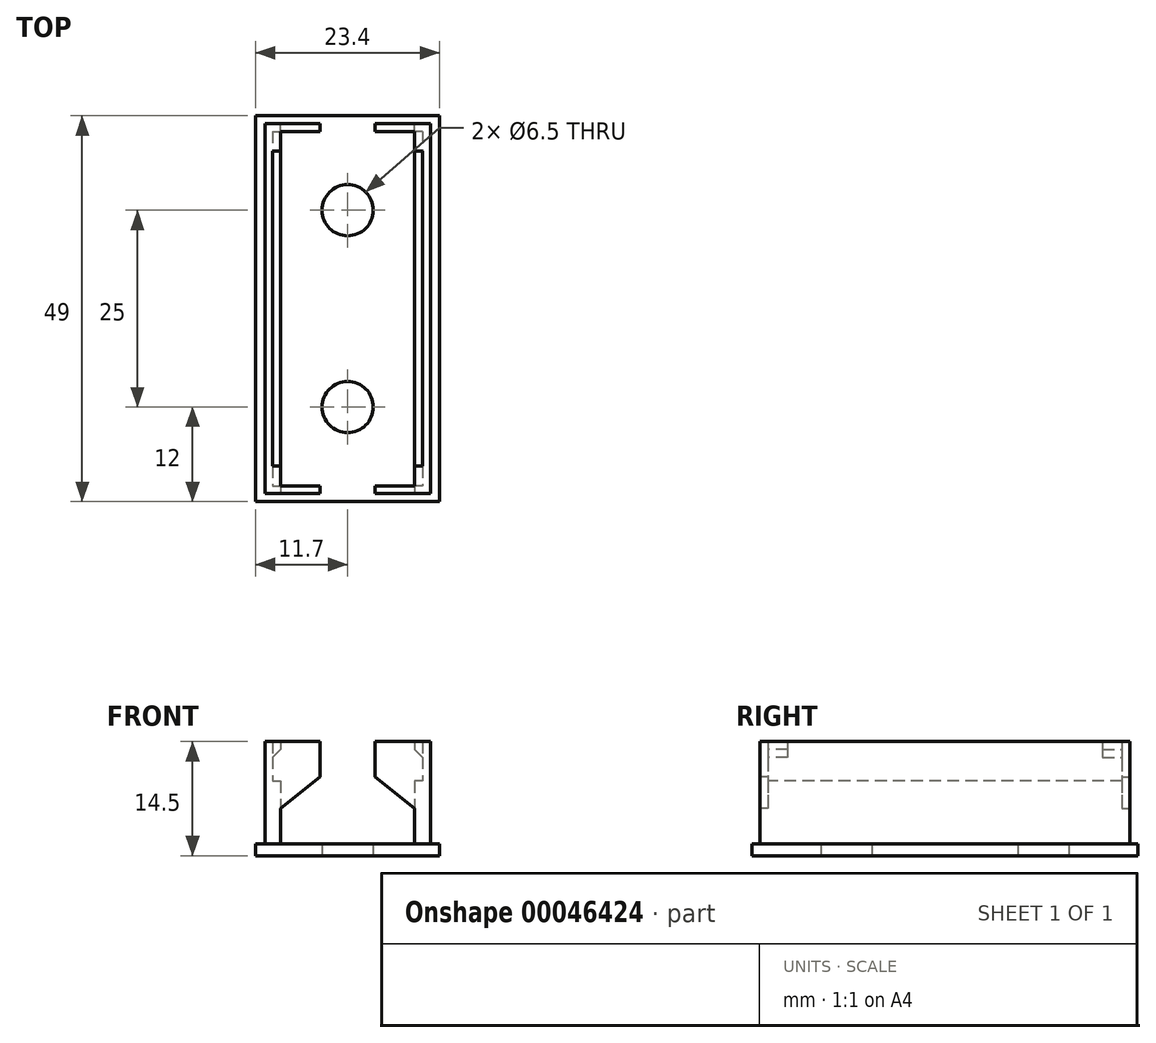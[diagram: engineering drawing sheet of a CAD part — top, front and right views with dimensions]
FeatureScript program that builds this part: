
annotation { "Feature Type Name" : "Feature", "Feature Type Description" : "" }
export const myFeature = defineFeature(function(context is Context, id is Id, definition is map)
    precondition{}
    {
        {
            var Q0;
            Q0=qCreatedBy(makeId("Top.planeOp"),FACE);
            var sketch = newSketch(context, id + "F0", { "sketchPlane" : qUnion([Q0])});
            skPoint(sketch, "E0.middle", {"position": v(0, 0) * mm});
            skCircle(sketch, "E1", {"center": v(0, 12.5) * mm, "radius": 3.25 * mm});
            skLineSegment(sketch, "E2", {"start": v(-11.7, 24.5) * mm, "end": v(-11.7, 0) * mm});
            skLineSegment(sketch, "E3", {"start": v(-11.7, 0) * mm, "end": v(0, 0) * mm});
            skLineSegment(sketch, "E4", {"start": v(-11.7, 24.5) * mm, "end": v(0, 24.5) * mm});
            skLineSegment(sketch, "E5", {"start": v(0, 24.5) * mm, "end": v(0, 0) * mm});
            skSolve(sketch);
        }
        {
            var Q0;
            Q0=makeQuery(id+"F0.imprint","IMPRINT",FACE,{"disambiguationData":[TD([[makeQuery(id+"F0.imprint","IMPRINT",EDGE,{"derivedFrom":sQuery(id+"F0.wireOp",EDGE,"E0.bottom")}),-1.0]])]});
            var Q1;
            Q1=makeQuery(id+"F0.imprint","IMPRINT",FACE,{"disambiguationData":[TD([[makeQuery(id+"F0.imprint","IMPRINT",EDGE,{"derivedFrom":sQuery(id+"F0.wireOp",EDGE,"E2")}),1.0]])]});
            extrude(context, id + "F1", {"entities" : qUnion([Q0, Q1]), "depth" : 1.5 * mm, "offsetDistance" : 25 * mm});
        }
        {
            var Q0;
            Q0=makeQuery(id+"F1.opExtrude","CAP_FACE",FACE,{"disambiguationData":[OSD([sQuery(id+"F0.wireOp",EDGE,"E0.bottom"),sQuery(id+"F0.wireOp",EDGE,"E0.top"),sQuery(id+"F0.wireOp",EDGE,"E0.left"),sQuery(id+"F0.wireOp",EDGE,"E0.right"),sQuery(id+"F0.wireOp",EDGE,"E1"),sQuery(id+"F0.wireOp",EDGE,"b4a6264c-28c6-449c-b6e5-1ad2d47b1fbf0.MirrorC")])],"isStart":false});
            var sketch = newSketch(context, id + "F2", { "sketchPlane" : qUnion([Q0])});
            skLineSegment(sketch, "E6.bottom", {"start": v(-10.5, 23.5) * mm, "end": v(-8.5, 23.5) * mm});
            skLineSegment(sketch, "E6.top", {"start": v(-10.5, 0) * mm, "end": v(-8.5, 0) * mm});
            skLineSegment(sketch, "E6.left", {"start": v(-10.5, 23.5) * mm, "end": v(-10.5, 0) * mm});
            skLineSegment(sketch, "E6.right", {"start": v(-8.5, 23.5) * mm, "end": v(-8.5, 0) * mm});
            skSolve(sketch);
        }
        {
            var Q0;
            Q0=makeQuery(id+"F2.imprint","IMPRINT",FACE,{"disambiguationData":[TD([[makeQuery(id+"F2.imprint","IMPRINT",EDGE,{"derivedFrom":sQuery(id+"F2.wireOp",EDGE,"4ac17364-d6f0-4829-a121-ceda3a2869c10.MirrorCS")}),1.0]])]});
            var Q1;
            Q1=makeQuery(id+"F2.imprint","IMPRINT",FACE,{"disambiguationData":[TD([[makeQuery(id+"F2.imprint","IMPRINT",EDGE,{"derivedFrom":sQuery(id+"F2.wireOp",EDGE,"E6.bottom")}),-1.0]])]});
            extrude(context, id + "F3", {"entities" : qUnion([Q0, Q1]), "operationType" : NewBodyOperationType.ADD, "depth" : 8 * mm, "offsetDistance" : 25 * mm});
        }
        {
            var Q0;
            Q0=makeQuery(id+"F3.opExtrude","CAP_FACE",FACE,{"disambiguationData":[OSD([sQuery(id+"F2.wireOp",EDGE,"E6.bottom"),sQuery(id+"F2.wireOp",EDGE,"E6.left"),sQuery(id+"F2.wireOp",EDGE,"E6.right"),sQuery(id+"F2.wireOp",EDGE,"4ac17364-d6f0-4829-a121-ceda3a2869c10.MirrorCS"),sQuery(id+"F2.wireOp",EDGE,"4ac17364-d6f0-4829-a121-ceda3a2869c12.MirrorCS"),sQuery(id+"F2.wireOp",EDGE,"4ac17364-d6f0-4829-a121-ceda3a2869c13.MirrorCS")])],"isStart":false});
            var sketch = newSketch(context, id + "F4", { "sketchPlane" : qUnion([Q0])});
            skLineSegment(sketch, "E7.bottom", {"start": v(-10.5, 23.5) * mm, "end": v(-9.5, 23.5) * mm});
            skLineSegment(sketch, "E7.top", {"start": v(-10.5, 0) * mm, "end": v(-9.5, 0) * mm});
            skLineSegment(sketch, "E7.left", {"start": v(-10.5, 23.5) * mm, "end": v(-10.5, 0) * mm});
            skLineSegment(sketch, "E7.right", {"start": v(-9.5, 23.5) * mm, "end": v(-9.5, 0) * mm});
            skSolve(sketch);
        }
        {
            var Q0;
            Q0=makeQuery(id+"F4.imprint","IMPRINT",FACE,{"disambiguationData":[TD([[makeQuery(id+"F4.imprint","IMPRINT",EDGE,{"derivedFrom":sQuery(id+"F4.wireOp",EDGE,"E7.bottom")}),-1.0]])]});
            extrude(context, id + "F5", {"entities" : qUnion([Q0]), "operationType" : NewBodyOperationType.ADD, "depth" : 5 * mm, "offsetDistance" : 25 * mm});
        }
        {
            var Q0;
            Q0=makeQuery(id+"F5.boolean.opBoolean","MERGE",FACE,{"derivedFrom":[makeQuery(id+"F3.opExtrude","SWEPT_FACE",FACE,{"disambiguationData":[OSD([sQuery(id+"F2.wireOp",EDGE,"E6.bottom")])]}),makeQuery(id+"F5.opExtrude","SWEPT_FACE",FACE,{"disambiguationData":[OSD([sQuery(id+"F4.wireOp",EDGE,"E7.bottom")])]})]});
            var sketch = newSketch(context, id + "F6", { "sketchPlane" : qUnion([Q0])});
            skLineSegment(sketch, "E8", {"start": v(9.5, 14.5) * mm, "end": v(3.5, 14.5) * mm});
            skLineSegment(sketch, "E9", {"start": v(3.5, 14.5) * mm, "end": v(3.5, 10) * mm});
            skLineSegment(sketch, "E10", {"start": v(3.5, 10) * mm, "end": v(8.5, 6) * mm});
            skLineSegment(sketch, "E11", {"start": v(8.5, 6) * mm, "end": v(8.5, 9.5) * mm});
            skLineSegment(sketch, "E12", {"start": v(8.5, 9.5) * mm, "end": v(9.5, 9.5) * mm});
            skLineSegment(sketch, "E13", {"start": v(9.5, 9.5) * mm, "end": v(9.5, 14.5) * mm});
            skSolve(sketch);
        }
        {
            var Q0;
            Q0=makeQuery(id+"F6.imprint","IMPRINT",FACE,{"disambiguationData":[TD([[makeQuery(id+"F6.imprint","IMPRINT",EDGE,{"derivedFrom":sQuery(id+"F6.wireOp",EDGE,"E8")}),1.0]])]});
            extrude(context, id + "F7", {"entities" : qUnion([Q0]), "operationType" : NewBodyOperationType.ADD, "oppositeDirection" : true, "depth" : 1 * mm, "offsetDistance" : 25 * mm});
        }
        {
            var Q0;
            Q0=makeQuery(id+"F7.opExtrude","CAP_FACE",FACE,{"disambiguationData":[OSD([sQuery(id+"F6.wireOp",EDGE,"E8"),sQuery(id+"F6.wireOp",EDGE,"E9"),sQuery(id+"F6.wireOp",EDGE,"E10"),sQuery(id+"F6.wireOp",EDGE,"E11"),sQuery(id+"F6.wireOp",EDGE,"E12"),sQuery(id+"F6.wireOp",EDGE,"E13")])],"isStart":false});
            var sketch = newSketch(context, id + "F8", { "sketchPlane" : qUnion([Q0])});
            skLineSegment(sketch, "E14", {"start": v(-9.5, 14.5) * mm, "end": v(-8.5, 14.5) * mm});
            skLineSegment(sketch, "E15", {"start": v(-8.5, 14.5) * mm, "end": v(-8.5, 13.5) * mm});
            skLineSegment(sketch, "E16", {"start": v(-8.5, 13.5) * mm, "end": v(-9.5, 12.5) * mm});
            skLineSegment(sketch, "E17", {"start": v(-9.5, 12.5) * mm, "end": v(-9.5, 14.5) * mm});
            skSolve(sketch);
        }
        {
            var Q0;
            Q0=makeQuery(id+"F8.imprint","IMPRINT",FACE,{"disambiguationData":[TD([[makeQuery(id+"F8.imprint","IMPRINT",EDGE,{"derivedFrom":sQuery(id+"F8.wireOp",EDGE,"E14")}),-1.0]])]});
            extrude(context, id + "F9", {"entities" : qUnion([Q0]), "operationType" : NewBodyOperationType.ADD, "depth" : 2.5 * mm, "offsetDistance" : 25 * mm});
        }
        {
            var Q0;
            Q0=makeQuery(id+"F1.opExtrude","SWEPT_BODY",BODY,{"disambiguationData":[OSD([sQuery(id+"F0.wireOp",EDGE,"E1"),sQuery(id+"F0.wireOp",EDGE,"E2"),sQuery(id+"F0.wireOp",EDGE,"E3"),sQuery(id+"F0.wireOp",EDGE,"E4"),sQuery(id+"F0.wireOp",EDGE,"E5")])]});
            var Q1;
            Q1=qCreatedBy(makeId("Front.planeOp"),FACE);
            mirror(context, id + "F10", {"operationType" : NewBodyOperationType.ADD, "entities" : qUnion([Q0]), "mirrorPlane" : qUnion([Q1])});
        }
        {
            var Q0;
            Q0=makeQuery(id+"F1.opExtrude","SWEPT_BODY",BODY,{"disambiguationData":[OSD([sQuery(id+"F0.wireOp",EDGE,"E1"),sQuery(id+"F0.wireOp",EDGE,"E2"),sQuery(id+"F0.wireOp",EDGE,"E3"),sQuery(id+"F0.wireOp",EDGE,"E4"),sQuery(id+"F0.wireOp",EDGE,"E5")])]});
            var Q1;
            Q1=qCreatedBy(makeId("Right.planeOp"),FACE);
            mirror(context, id + "F11", {"operationType" : NewBodyOperationType.ADD, "entities" : qUnion([Q0]), "mirrorPlane" : qUnion([Q1])});
        }
    });
